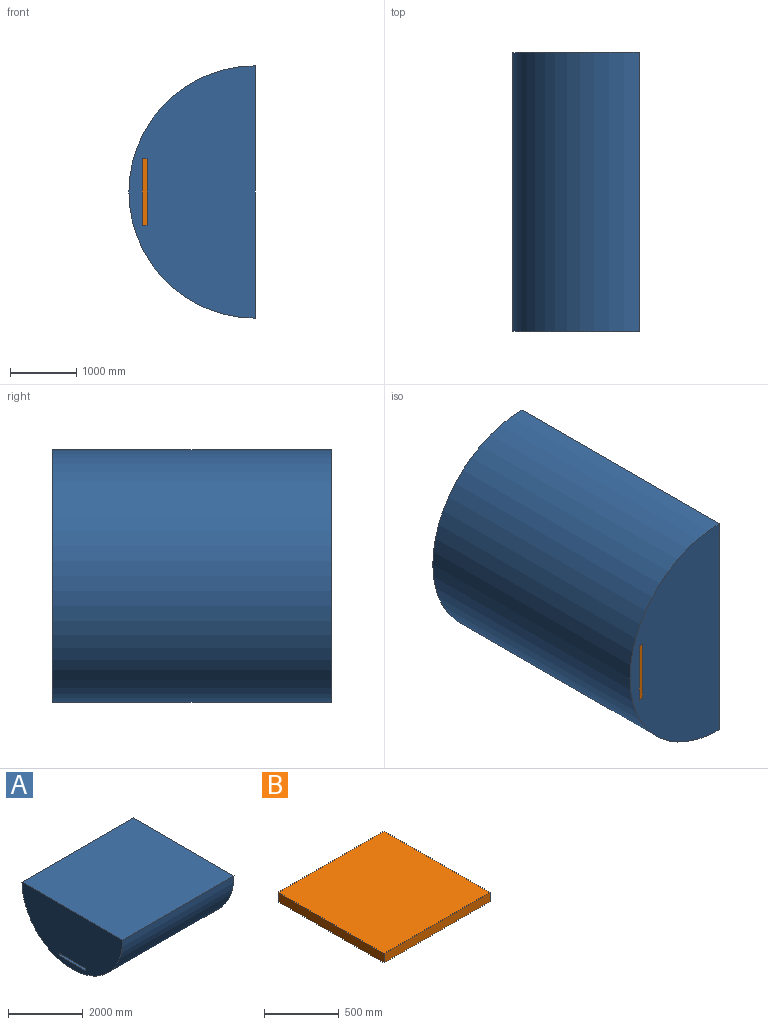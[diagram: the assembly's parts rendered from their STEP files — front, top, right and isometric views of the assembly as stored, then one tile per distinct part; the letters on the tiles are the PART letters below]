
ASSEMBLY  parts=2 mates=1
PART A: 9 faces, bbox 4200x3800x1900 mm
  f0: cylinder r=1900mm len=4200mm, axis (-1,0,0), area 25069909.4mm2, adj f1,f2,f8
  f1: plane 3800x1900mm, normal (1,0,0), area 5670574.7mm2, adj f0,f8
  f2: plane 3800x1900mm, normal (-1,0,0), area 5595574.7mm2, adj f0,f3,f5,f6,f7,f8
  f3: plane 1000x75mm, normal (0,1,0), area 75000mm2, adj f2,f4,f6,f7
  f4: plane 1000x75mm, normal (-1,0,0), area 75000mm2, adj f3,f5,f6,f7
  f5: plane 1000x75mm, normal (0,-1,0), area 75000mm2, adj f2,f4,f6,f7
  f6: plane 1000x1000mm, normal (0,0,1), area 1000000mm2, adj f2,f3,f4,f5
  f7: plane 1000x1000mm, normal (0,0,-1), area 1000000mm2, adj f2,f3,f4,f5
  f8: plane 4200x3800mm, normal (0,0,1), area 15960000mm2, adj f0,f1,f2
PART B: 6 faces, bbox 1000x1000x75 mm
  f0: plane 1000x75mm, normal (-1,0,0), area 75000mm2, adj f1,f3,f4,f5
  f1: plane 1000x75mm, normal (0,-1,0), area 75000mm2, adj f0,f2,f4,f5
  f2: plane 1000x75mm, normal (1,0,0), area 75000mm2, adj f1,f3,f4,f5
  f3: plane 1000x75mm, normal (0,1,0), area 75000mm2, adj f0,f2,f4,f5
  f4: plane 1000x1000mm, normal (0,0,1), area 1000000mm2, adj f0,f1,f2,f3
  f5: plane 1000x1000mm, normal (0,0,-1), area 1000000mm2, adj f0,f1,f2,f3
PLACE A rot(axis=(0.58,0.58,0.58),120deg) t=(-1700,0,-500)mm
PLACE B rot(axis=(-0.58,-0.58,0.58),120deg) t=(-1625,0,500)mm
MATE fastened A.f6 <-> B.f4  axis (1,0,0) through (-1700,500,0)mm
